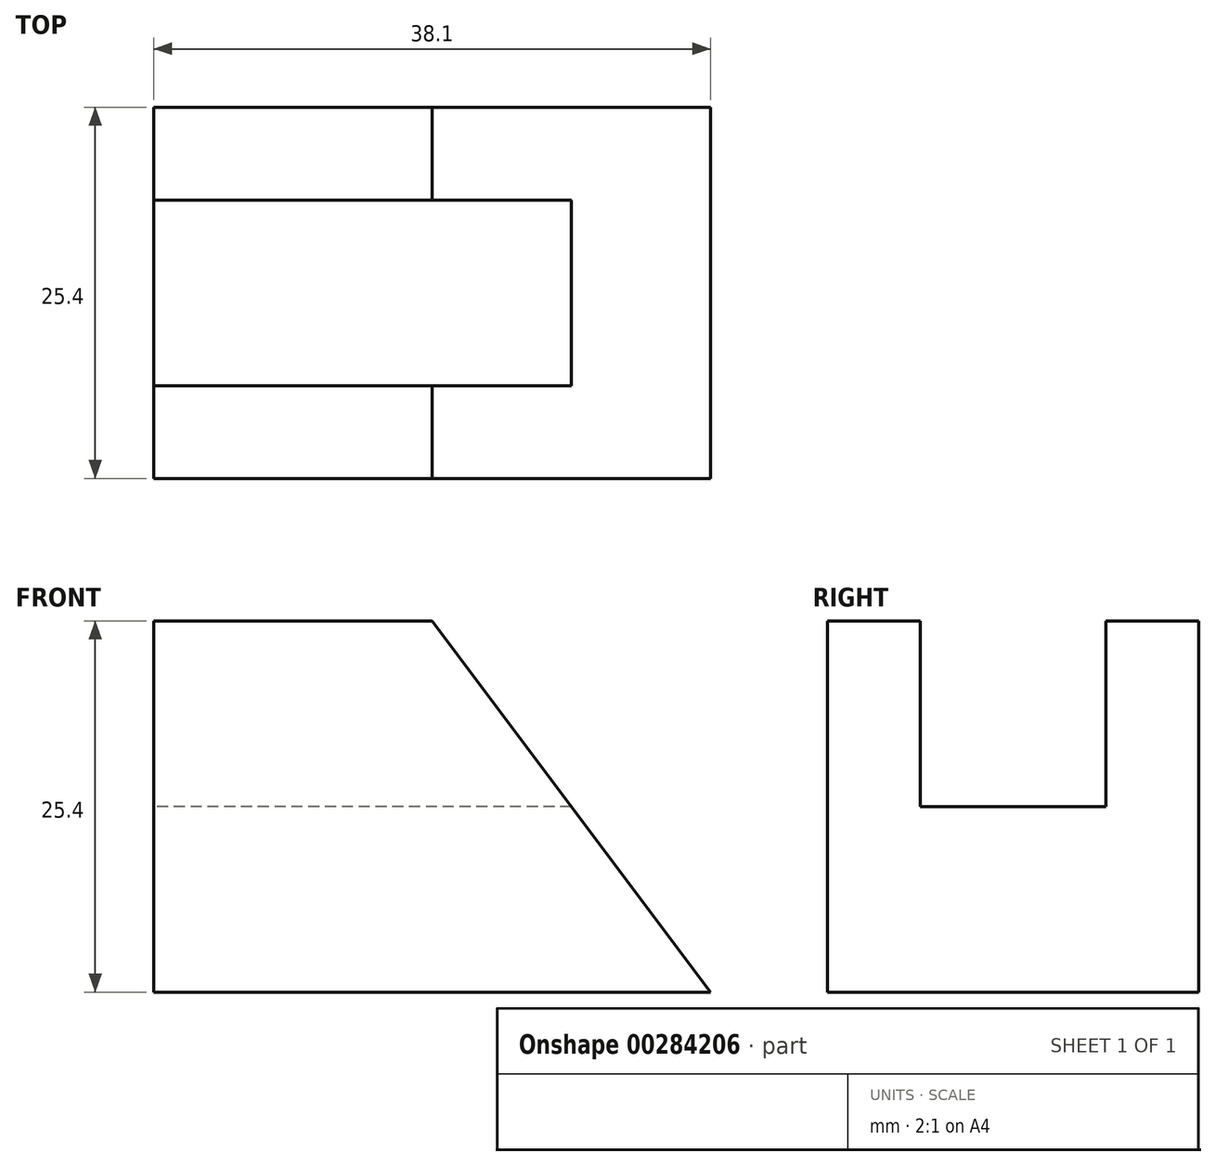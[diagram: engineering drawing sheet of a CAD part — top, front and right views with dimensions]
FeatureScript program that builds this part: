
annotation { "Feature Type Name" : "Feature", "Feature Type Description" : "" }
export const myFeature = defineFeature(function(context is Context, id is Id, definition is map)
    precondition{}
    {
        {
            var Q0;
            Q0=qCreatedBy(makeId("Front.planeOp"),FACE);
            var sketch = newSketch(context, id + "F0", { "sketchPlane" : qUnion([Q0])});
            skLineSegment(sketch, "E0", {"start": v(0, 0) * mm, "end": v(0, 25.4) * mm});
            skLineSegment(sketch, "E1", {"start": v(0, 25.4) * mm, "end": v(19.05, 25.4) * mm});
            skLineSegment(sketch, "E2", {"start": v(19.05, 25.4) * mm, "end": v(38.1, 0) * mm});
            skLineSegment(sketch, "E3", {"start": v(38.1, 0) * mm, "end": v(0, 0) * mm});
            skSolve(sketch);
        }
        {
            var Q0;
            Q0 = qSketchRegion(id + "F0", true);
            extrude(context, id + "F1", {"entities" : qUnion([Q0]), "oppositeDirection" : true, "depth" : 25.4 * mm});
        }
        {
            var Q0;
            Q0=makeQuery(id+"F1.opExtrude","SWEPT_FACE",FACE,{"disambiguationData":[OSD([sQuery(id+"F0.wireOp",EDGE,"E0")])]});
            var sketch = newSketch(context, id + "F2", { "sketchPlane" : qUnion([Q0])});
            skLineSegment(sketch, "E4", {"start": v(-19.05, 25.4) * mm, "end": v(-19.05, 12.7) * mm});
            skLineSegment(sketch, "E5", {"start": v(-19.05, 12.7) * mm, "end": v(-6.35, 12.7) * mm});
            skLineSegment(sketch, "E6", {"start": v(-6.35, 12.7) * mm, "end": v(-6.35, 25.4) * mm});
            skLineSegment(sketch, "E7", {"start": v(-6.35, 25.4) * mm, "end": v(-19.05, 25.4) * mm});
            skSolve(sketch);
        }
        {
            var Q0;
            Q0=makeQuery(id+"F2.imprint","IMPRINT",FACE,{"disambiguationData":[TD([[makeQuery(id+"F2.imprint","IMPRINT",EDGE,{"derivedFrom":sQuery(id+"F2.wireOp",EDGE,"E4")}),1.0]])]});
            var Q1;
            Q1=sQuery(id+"F2.wireOp",EDGE,"E7");
            var Q2;
            Q2=sQuery(id+"F2.wireOp",EDGE,"E4");
            var Q3;
            Q3=sQuery(id+"F2.wireOp",EDGE,"E6");
            var Q4;
            Q4=sQuery(id+"F2.wireOp",EDGE,"E5");
            extrude(context, id + "F3", {"entities" : qUnion([Q0]), "operationType" : NewBodyOperationType.REMOVE, "surfaceEntities" : qUnion([Q1, Q2, Q3, Q4]), "endBound" : BoundingType.THROUGH_ALL, "oppositeDirection" : true, "depth" : 25.4 * mm});
        }
    });
